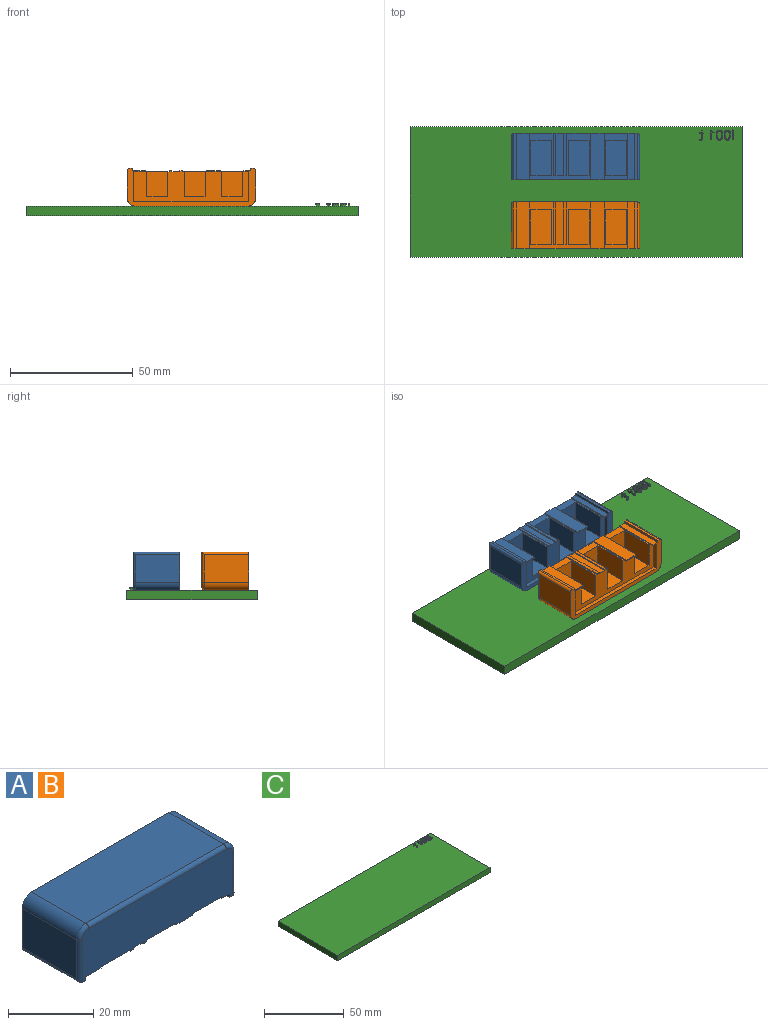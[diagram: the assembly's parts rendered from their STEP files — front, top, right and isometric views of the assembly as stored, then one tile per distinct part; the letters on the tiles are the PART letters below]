
ASSEMBLY  parts=3 mates=2
PART A: 55 faces, bbox 52.6x19.1x15.7 mm
  f0: plane 17.4x9.65mm, normal (0,0,-1), area 47.8mm2, adj f5,f21,f24,f27,f38,f39,f40
  f1: plane 17.4x3.18mm, normal (0,0,-1), area 55.2mm2, adj f5,f24,f25,f26
  f2: plane 17.4x9.65mm, normal (0,0,-1), area 47.8mm2, adj f5,f22,f23,f24,f34,f35,f36
  f3: plane 17.4x9.65mm, normal (0,0,-1), area 47.8mm2, adj f5,f24,f28,f29,f30,f31,f32
  f4: plane 5.59x0.43mm, normal (0,1,0), area 2.4mm2, adj f7,f22,f28,f43
  f5: plane 50.04x14.44mm, normal (0,-1,0), area 657.8mm2, adj f0,f1,f2,f3,f6,f7,f8,f9
  f6: plane 19.05x2.67mm, normal (0,0,-1), area 50.8mm2, adj f5,f15,f19,f29
  f7: plane 19.05x5.59mm, normal (0,0,-1), area 106.5mm2, adj f4,f5,f22,f28
  f8: plane 19.05x5.21mm, normal (0,0,-1), area 99.2mm2, adj f5,f15,f18,f21
  f9: plane 17.4x1.21mm, normal (0,0,-1), area 21mm2, adj f5,f23,f24,f25
  f10: plane 19.05x1.02mm, normal (0,0,-1), area 19.4mm2, adj f5,f15,f19,f48
  f11: plane 18.03x11.26mm, normal (-1,0,0), area 203.1mm2, adj f15,f17,f52,f54
  f12: plane 19.05x1.02mm, normal (0,0,-1), area 19.4mm2, adj f5,f15,f18,f52
  f13: plane 18.03x11.26mm, normal (1,0,0), area 203.1mm2, adj f15,f16,f48,f49
  f14: plane 45.72x18.03mm, normal (0,0,1), area 824.5mm2, adj f15,f16,f17,f51
  f15: plane 52.07x15.45mm, normal (0,1,0), area 164.3mm2, adj f6,f8,f10,f11,f12,f13,f14,f16
  f16: cylinder r=3.17mm len=18.03mm, axis (0,1,0), area 89.9mm2, adj f13,f14,f15,f50
  f17: cylinder r=3.17mm len=18.03mm, axis (0,-1,0), area 89.9mm2, adj f11,f14,f15,f53
  f18: plane 19.05x1.02mm, normal (1,0,0), area 19.4mm2, adj f5,f8,f12,f15
  f19: plane 19.05x1.02mm, normal (-1,0,0), area 19.4mm2, adj f5,f6,f10,f15
  f20: plane 17.4x1.21mm, normal (0,0,-1), area 21mm2, adj f5,f24,f26,f27
  f21: plane 19.05x0.43mm, normal (1,0,0), area 8.2mm2, adj f0,f5,f8,f15,f42
  f22: plane 19.05x0.43mm, normal (-1,0,0), area 8.2mm2, adj f2,f4,f5,f7,f43
  f23: plane 17.4x0.43mm, normal (1,0,0), area 7.5mm2, adj f2,f5,f9,f24
  f24: plane 46.57x12.66mm, normal (0,1,0), area 311.2mm2, adj f0,f1,f2,f3,f9,f20,f23,f25
  f25: plane 17.4x0.43mm, normal (-1,0,0), area 7.5mm2, adj f1,f5,f9,f24
  f26: plane 17.4x0.43mm, normal (1,0,0), area 7.5mm2, adj f1,f5,f20,f24
  f27: plane 17.4x0.43mm, normal (-1,0,0), area 7.5mm2, adj f0,f5,f20,f24
  f28: plane 19.05x0.43mm, normal (1,0,0), area 8.2mm2, adj f3,f4,f5,f7,f43
  f29: plane 19.05x0.43mm, normal (-1,0,0), area 8.2mm2, adj f3,f5,f6,f15,f44
  f30: plane 10.23x8.45mm, normal (0,1,0), area 86.4mm2, adj f3,f31,f32,f33
  f31: plane 14.22x10.23mm, normal (1,0,0), area 145.6mm2, adj f3,f24,f30,f33
  f32: plane 14.22x10.23mm, normal (-1,0,0), area 145.6mm2, adj f3,f24,f30,f33
  f33: plane 14.22x8.45mm, normal (0,0,-1), area 120.2mm2, adj f24,f30,f31,f32
  f34: plane 10.23x8.45mm, normal (0,1,0), area 86.4mm2, adj f2,f35,f36,f37
  f35: plane 14.22x10.23mm, normal (1,0,0), area 145.6mm2, adj f2,f24,f34,f37
  f36: plane 14.22x10.23mm, normal (-1,0,0), area 145.6mm2, adj f2,f24,f34,f37
  f37: plane 14.22x8.45mm, normal (0,0,-1), area 120.2mm2, adj f24,f34,f35,f36
  f38: plane 10.23x8.45mm, normal (0,1,0), area 86.4mm2, adj f0,f39,f40,f41
  f39: plane 14.22x10.23mm, normal (1,0,0), area 145.6mm2, adj f0,f24,f38,f41
  f40: plane 14.22x10.23mm, normal (-1,0,0), area 145.6mm2, adj f0,f24,f38,f41
  f41: plane 14.22x8.45mm, normal (0,0,-1), area 120.2mm2, adj f24,f38,f39,f40
  f42: plane 4.66x1.65mm, normal (0,0,1), area 7.7mm2, adj f15,f21,f24,f45
  f43: plane 5.59x1.65mm, normal (0,0,1), area 9.2mm2, adj f4,f22,f24,f28
  f44: plane 1.78x1.65mm, normal (0,0,1), area 2.9mm2, adj f15,f24,f29,f47
  f45: plane 12.23x1.65mm, normal (1,0,0), area 20.2mm2, adj f15,f24,f42,f46
  f46: plane 46.57x1.65mm, normal (0,0,-1), area 76.9mm2, adj f15,f24,f45,f47
  f47: plane 12.23x1.65mm, normal (-1,0,0), area 20.2mm2, adj f15,f24,f44,f46
  f48: cylinder r=1.02mm len=19.05mm, axis (0,-1,0), area 29.8mm2, adj f10,f13,f15,f49
  f49: cylinder r=1.02mm len=12.28mm, axis (0,0,1), area 19mm2, adj f5,f13,f48,f50
  f50: torus R=2.16mm, axis (0,-1,0), area 7mm2, adj f5,f16,f49,f51
  f51: cylinder r=1.02mm len=45.72mm, axis (-1,0,0), area 73mm2, adj f5,f14,f50,f53
  f52: cylinder r=1.02mm len=19.05mm, axis (0,1,0), area 29.8mm2, adj f11,f12,f15,f54
  f53: torus R=2.16mm, axis (0,-1,0), area 7mm2, adj f5,f17,f51,f54
  f54: cylinder r=1.02mm len=12.28mm, axis (0,0,-1), area 19mm2, adj f5,f11,f52,f53
PART B: same geometry as A
PART C: 86 faces, bbox 135x53x5 mm
  f0: plane 135x53mm, normal (0,0,1), area 7131.1mm2, adj f1,f2,f3,f4,f6,f7,f8,f9
  f1: plane 53x4mm, normal (-1,0,0), area 212mm2, adj f0,f2,f4,f5
  f2: plane 135x4mm, normal (0,-1,0), area 540mm2, adj f0,f1,f3,f5
  f3: plane 53x4mm, normal (1,0,0), area 212mm2, adj f0,f2,f4,f5
  f4: plane 135x4mm, normal (0,1,0), area 540mm2, adj f0,f1,f3,f5
  f5: plane 135x53mm, normal (0,0,-1), area 7155mm2, adj f1,f2,f3,f4
  f6: plane 2.97x1mm, normal (-1,0,0), area 3mm2, adj f0,f7,f9,f10
  f7: plane 1x0.45mm, normal (0,-1,0), area 0.5mm2, adj f0,f6,f8,f10
  f8: plane 2.97x1mm, normal (1,0,0), area 3mm2, adj f0,f7,f9,f10
  f9: plane 1x0.45mm, normal (0,1,0), area 0.5mm2, adj f0,f6,f8,f10
  f10: plane 2.97x0.45mm, normal (0,0,1), area 1.3mm2, adj f6,f7,f8,f9
  f11: extruded ~1x0.23mm, area 0.2mm2, adj f0,f12,f18,f19
  f12: extruded ~1x0.23mm, area 0.2mm2, adj f0,f11,f13,f19
  f13: extruded ~1x0.19mm, area 0.2mm2, adj f0,f12,f14,f19
  f14: extruded ~1x0.19mm, area 0.2mm2, adj f0,f13,f15,f19
  f15: extruded ~1x0.23mm, area 0.2mm2, adj f0,f14,f16,f19
  f16: extruded ~1x0.23mm, area 0.2mm2, adj f0,f15,f17,f19
  f17: extruded ~1x0.19mm, area 0.2mm2, adj f0,f16,f18,f19
  f18: extruded ~1x0.19mm, area 0.2mm2, adj f0,f11,f17,f19
  f19: plane 0.6x0.53mm, normal (0,0,1), area 0.3mm2, adj f11,f12,f13,f14,f15,f16,f17,f18
  f20: extruded ~1.52x1mm, area 1.6mm2, adj f0,f21,f35,f36
  f21: extruded ~1.54x1mm, area 1.6mm2, adj f0,f20,f22,f36
  f22: extruded ~1x0.99mm, area 1.2mm2, adj f0,f21,f23,f36
  f23: extruded ~1x0.97mm, area 1.2mm2, adj f0,f22,f24,f36
  f24: extruded ~1.52x1mm, area 1.6mm2, adj f0,f23,f25,f36
  f25: extruded ~1.54x1mm, area 1.6mm2, adj f0,f24,f26,f36
  f26: extruded ~1x0.98mm, area 1.2mm2, adj f0,f25,f35,f36
  f27: extruded ~1.26x1mm, area 1.3mm2, adj f28,f34,f36,f37
  f28: extruded ~1.26x1mm, area 1.3mm2, adj f27,f29,f36,f37
  f29: extruded ~1x0.65mm, area 0.8mm2, adj f28,f30,f36,f37
  f30: extruded ~1x0.65mm, area 0.8mm2, adj f29,f31,f36,f37
  f31: extruded ~1.26x1mm, area 1.3mm2, adj f30,f32,f36,f37
  f32: extruded ~1.25x1mm, area 1.3mm2, adj f31,f33,f36,f37
  f33: extruded ~1x0.65mm, area 0.8mm2, adj f32,f34,f36,f37
  f34: extruded ~1x0.65mm, area 0.8mm2, adj f27,f33,f36,f37
  f35: extruded ~1x0.98mm, area 1.2mm2, adj f0,f20,f26,f36
  f36: plane 4.08x2.62mm, normal (0,0,1), area 4.2mm2, adj f20,f21,f22,f23,f24,f25,f26,f27
  f37: plane 3.3x1.71mm, normal (0,0,1), area 4.8mm2, adj f27,f28,f29,f30,f31,f32,f33,f34
  f38: extruded ~1.52x1mm, area 1.6mm2, adj f0,f39,f53,f54
  f39: extruded ~1.54x1mm, area 1.6mm2, adj f0,f38,f40,f54
  f40: extruded ~1x0.99mm, area 1.2mm2, adj f0,f39,f41,f54
  f41: extruded ~1x0.97mm, area 1.2mm2, adj f0,f40,f42,f54
  f42: extruded ~1.52x1mm, area 1.6mm2, adj f0,f41,f43,f54
  f43: extruded ~1.54x1mm, area 1.6mm2, adj f0,f42,f44,f54
  f44: extruded ~1x0.98mm, area 1.2mm2, adj f0,f43,f53,f54
  f45: extruded ~1.26x1mm, area 1.3mm2, adj f46,f52,f54,f55
  f46: extruded ~1.26x1mm, area 1.3mm2, adj f45,f47,f54,f55
  f47: extruded ~1x0.65mm, area 0.8mm2, adj f46,f48,f54,f55
  f48: extruded ~1x0.65mm, area 0.8mm2, adj f47,f49,f54,f55
  f49: extruded ~1.26x1mm, area 1.3mm2, adj f48,f50,f54,f55
  f50: extruded ~1.25x1mm, area 1.3mm2, adj f49,f51,f54,f55
  f51: extruded ~1x0.65mm, area 0.8mm2, adj f50,f52,f54,f55
  f52: extruded ~1x0.65mm, area 0.8mm2, adj f45,f51,f54,f55
  f53: extruded ~1x0.98mm, area 1.2mm2, adj f0,f38,f44,f54
  f54: plane 4.08x2.62mm, normal (0,0,1), area 4.2mm2, adj f38,f39,f40,f41,f42,f43,f44,f45
  f55: plane 3.3x1.71mm, normal (0,0,1), area 4.8mm2, adj f45,f46,f47,f48,f49,f50,f51,f52
  f56: plane 3.97x1mm, normal (-1,0,0), area 4mm2, adj f0,f57,f64,f65
  f57: plane 1x0.44mm, normal (0,-1,0), area 0.4mm2, adj f0,f56,f58,f65
  f58: plane 2.83x1mm, normal (1,0,0), area 2.8mm2, adj f0,f57,f59,f65
  f59: extruded ~1x0.67mm, area 0.7mm2, adj f0,f58,f60,f65
  f60: extruded ~1x0.13mm, area 0.2mm2, adj f0,f59,f61,f65
  f61: extruded ~1x0.65mm, area 0.8mm2, adj f0,f60,f62,f65
  f62: plane 1x0.31mm, normal (0.79,-0.61,0), area 0.4mm2, adj f0,f61,f63,f65
  f63: plane 1.05x1mm, normal (0.61,0.79,0), area 1.3mm2, adj f0,f62,f64,f65
  f64: plane 1x0.38mm, normal (0,1,0), area 0.4mm2, adj f0,f56,f63,f65
  f65: plane 3.97x1.43mm, normal (0,0,1), area 2.2mm2, adj f56,f57,f58,f59,f60,f61,f62,f63
  f66: extruded ~1x0.35mm, area 0.4mm2, adj f0,f67,f84,f85
  f67: extruded ~1x0.23mm, area 0.2mm2, adj f0,f66,f68,f85
  f68: extruded ~1x0.18mm, area 0.2mm2, adj f0,f67,f69,f85
  f69: plane 1x0.34mm, normal (-1,0,0), area 0.3mm2, adj f0,f68,f70,f85
  f70: extruded ~1x0.22mm, area 0.2mm2, adj f0,f69,f71,f85
  f71: extruded ~1x0.26mm, area 0.3mm2, adj f0,f70,f72,f85
  f72: extruded ~1x0.91mm, area 1.4mm2, adj f0,f71,f73,f85
  f73: plane 1.77x1mm, normal (1,0,0), area 1.8mm2, adj f0,f72,f74,f85
  f74: plane 1x0.43mm, normal (0,-1,0), area 0.4mm2, adj f0,f73,f75,f85
  f75: plane 1x0.22mm, normal (1,0,0), area 0.2mm2, adj f0,f74,f76,f85
  f76: plane 1x0.43mm, normal (0.4,0.92,0), area 0.5mm2, adj f0,f75,f77,f85
  f77: plane 1x0.63mm, normal (0.96,0.29,0), area 0.7mm2, adj f0,f76,f78,f85
  f78: plane 1x0.26mm, normal (0,1,0), area 0.3mm2, adj f0,f77,f79,f85
  f79: plane 1x0.69mm, normal (-1,0,0), area 0.7mm2, adj f0,f78,f80,f85
  f80: plane 1x0.86mm, normal (0,1,0), area 0.9mm2, adj f0,f79,f81,f85
  f81: plane 1x0.35mm, normal (-1,0,0), area 0.3mm2, adj f0,f80,f82,f85
  f82: plane 1x0.86mm, normal (0,-1,0), area 0.9mm2, adj f0,f81,f83,f85
  f83: plane 1.75x1mm, normal (-1,0,0), area 1.7mm2, adj f0,f82,f84,f85
  f84: extruded ~1x0.41mm, area 0.4mm2, adj f0,f66,f83,f85
  f85: plane 3.72x1.76mm, normal (0,0,1), area 2.3mm2, adj f66,f67,f68,f69,f70,f71,f72,f73
PLACE A rot(axis=(1,0,0),180deg) t=(-39,0.49,16.95)mm
PLACE B rot(axis=(1,0,0),180deg) t=(-39,-27.51,16.95)mm
PLACE C t=(-20.26,10.04,-2.5)mm
MATE fastened B.f14 <-> C.f0  axis (0,0,-1) through (-12.96,-37.54,1.5)mm
MATE fastened A.f14 <-> C.f0  axis (0,0,-1) through (-12.96,-9.54,1.5)mm
